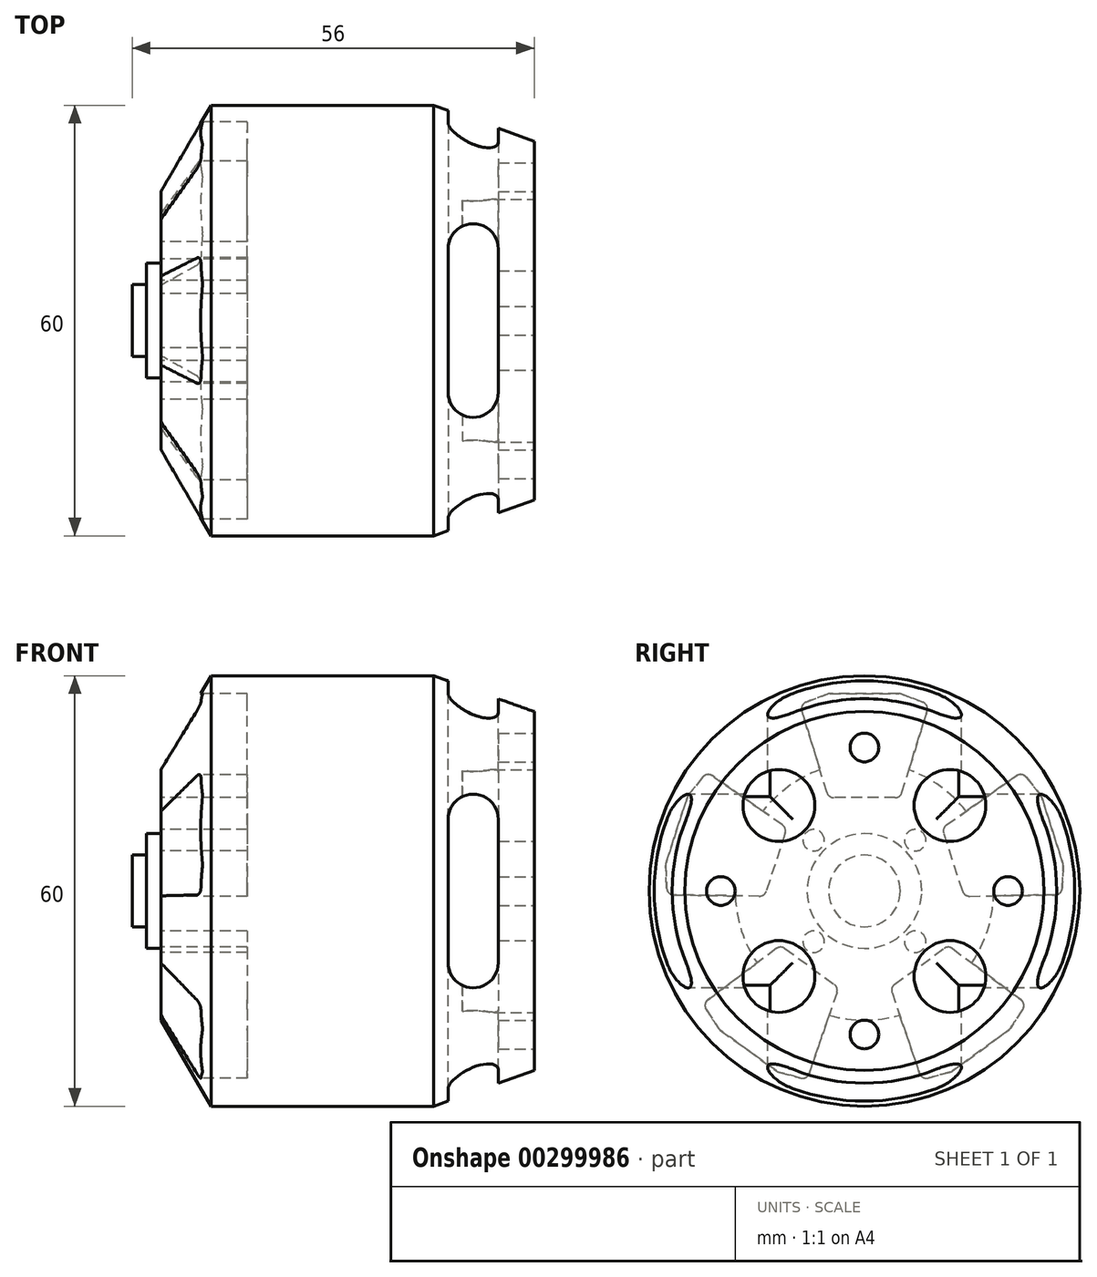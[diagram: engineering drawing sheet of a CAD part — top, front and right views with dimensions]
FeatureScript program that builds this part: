
annotation { "Feature Type Name" : "Feature", "Feature Type Description" : "" }
export const myFeature = defineFeature(function(context is Context, id is Id, definition is map)
    precondition{}
    {
        {
            var Q0;
            Q0=qCreatedBy(makeId("Right.planeOp"),FACE);
            var sketch = newSketch(context, id + "F0", { "sketchPlane" : qUnion([Q0])});
            skCircle(sketch, "E0", {"center": v(0, 0) * mm, "radius": 30 * mm});
            skSolve(sketch);
        }
        {
            var Q0;
            Q0 = qSketchRegion(id + "F0", true);
            extrude(context, id + "F1", {"entities" : qUnion([Q0]), "endBound" : BoundingType.SYMMETRIC, "depth" : 28 * mm, "offsetDistance" : 25 * mm});
        }
        {
            var Q0;
            Q0=qCreatedBy(makeId("Top.planeOp"),FACE);
            var sketch = newSketch(context, id + "F2", { "sketchPlane" : qUnion([Q0])});
            skLineSegment(sketch, "E1", {"start": v(14, 0) * mm, "end": v(28, 0) * mm});
            skLineSegment(sketch, "E2", {"start": v(14, 0) * mm, "end": v(14, 30) * mm});
            skLineSegment(sketch, "E3", {"start": v(14, 30) * mm, "end": v(28, 25) * mm});
            skLineSegment(sketch, "E4", {"start": v(28, 0) * mm, "end": v(28, 25) * mm});
            skLineSegment(sketch, "E5", {"start": v(-14, 0) * mm, "end": v(-24, 0) * mm});
            skLineSegment(sketch, "E6", {"start": v(-24, 0) * mm, "end": v(-24, 18) * mm});
            skLineSegment(sketch, "E7", {"start": v(-14, 0) * mm, "end": v(-14, 30) * mm});
            skLineSegment(sketch, "E8", {"start": v(-14, 30) * mm, "end": v(-17, 30) * mm});
            skLineSegment(sketch, "E9", {"start": v(-17, 30) * mm, "end": v(-24, 18) * mm});
            skLineSegment(sketch, "E10", {"start": v(-24, 0) * mm, "end": v(-26, 0) * mm});
            skLineSegment(sketch, "E11", {"start": v(-26, 0) * mm, "end": v(-26, 8) * mm});
            skLineSegment(sketch, "E12", {"start": v(-26, 8) * mm, "end": v(-24, 8) * mm});
            skLineSegment(sketch, "E13", {"start": v(-26, 0) * mm, "end": v(-28, 0) * mm});
            skLineSegment(sketch, "E14", {"start": v(-28, 0) * mm, "end": v(-28, 5) * mm});
            skLineSegment(sketch, "E15", {"start": v(-28, 5) * mm, "end": v(-26, 5) * mm});
            skSolve(sketch);
        }
        {
            var Q0;
            Q0 = qSketchRegion(id + "F2", true);
            var Q1;
            Q1=sQuery(id+"F2.wireOp",EDGE,"E1");
            revolve(context, id + "F3", {"operationType" : NewBodyOperationType.ADD, "entities" : qUnion([Q0]), "axis" : qUnion([Q1]), "revolveType" : RevolveType.FULL});
        }
        {
            var Q0;
            Q0=makeQuery(id+"F3.opRevolve","SWEPT_FACE",FACE,{"disambiguationData":[OSD([sQuery(id+"F2.wireOp",EDGE,"E4")])]});
            var sketch = newSketch(context, id + "F4", { "sketchPlane" : qUnion([Q0])});
            skCircle(sketch, "E16", {"center": v(0, 20) * mm, "radius": 2 * mm});
            skCircle(sketch, "E17", {"center": v(20, 0) * mm, "radius": 2 * mm});
            skCircle(sketch, "E18", {"center": v(0, -20) * mm, "radius": 2 * mm});
            skCircle(sketch, "E19", {"center": v(-20, 0) * mm, "radius": 2 * mm});
            skLineSegment(sketch, "E20", {"start": v(0, 0) * mm, "end": v(-11.92, 11.92) * mm});
            skCircle(sketch, "E21", {"center": v(-11.92, 11.92) * mm, "radius": 5 * mm});
            skCircle(sketch, "E22.1.0", {"center": v(-11.92, -11.92) * mm, "radius": 5 * mm});
            skCircle(sketch, "E22.2.0", {"center": v(11.92, -11.92) * mm, "radius": 5 * mm});
            skCircle(sketch, "E22.3.0", {"center": v(11.92, 11.92) * mm, "radius": 5 * mm});
            skPoint(sketch, "E22.center", {"position": v(0, 0) * mm});
            skSolve(sketch);
        }
        {
            var Q0;
            Q0 = qSketchRegion(id + "F4", true);
            extrude(context, id + "F5", {"entities" : qUnion([Q0]), "operationType" : NewBodyOperationType.REMOVE, "oppositeDirection" : true, "depth" : 10 * mm, "offsetDistance" : 25 * mm});
        }
        {
            var Q0;
            Q0=makeQuery(id+"F3.opRevolve","SWEPT_FACE",FACE,{"disambiguationData":[OSD([sQuery(id+"F2.wireOp",EDGE,"E6")])]});
            var sketch = newSketch(context, id + "F6", { "sketchPlane" : qUnion([Q0])});
            skLineSegment(sketch, "E23", {"start": v(0, 0) * mm, "end": v(7.07, 7.07) * mm});
            skCircle(sketch, "E24", {"center": v(7.07, 7.07) * mm, "radius": 1.5 * mm});
            skCircle(sketch, "E25.1.0", {"center": v(-7.07, 7.07) * mm, "radius": 1.5 * mm});
            skCircle(sketch, "E25.2.0", {"center": v(-7.07, -7.07) * mm, "radius": 1.5 * mm});
            skCircle(sketch, "E25.3.0", {"center": v(7.07, -7.07) * mm, "radius": 1.5 * mm});
            skPoint(sketch, "E25.center", {"position": v(0, 0) * mm});
            skLineSegment(sketch, "E26.bottom", {"start": v(-4.26, 13) * mm, "end": v(4.26, 13) * mm});
            skLineSegment(sketch, "E26.top", {"start": v(-4.82, 27.5) * mm, "end": v(4.82, 27.5) * mm});
            skLineSegment(sketch, "E26.left", {"start": v(-5, 13) * mm, "end": v(-5, 27.5) * mm});
            skLineSegment(sketch, "E26.right", {"start": v(5, 13) * mm, "end": v(5, 27.5) * mm});
            skLineSegment(sketch, "E27", {"start": v(5.22, 13.7) * mm, "end": v(8.72, 25.1) * mm});
            skLineSegment(sketch, "E28", {"start": v(8.12, 26.33) * mm, "end": v(5.17, 27.44) * mm});
            skLineSegment(sketch, "E29", {"start": v(-5.22, 13.7) * mm, "end": v(-8.72, 25.1) * mm});
            skLineSegment(sketch, "E30", {"start": v(-8.12, 26.33) * mm, "end": v(-5.17, 27.44) * mm});
            skPoint(sketch, "E31.visualSharp", {"position": v(9, 26) * mm});
            skArc(sketch, "E31.filletArc", {"start": v(8.72, 25.1) * mm, "mid": v(8.66, 25.84) * mm, "end": v(8.12, 26.33) * mm});
            skPoint(sketch, "E32.visualSharp", {"position": v(-9, 26) * mm});
            skArc(sketch, "E32.filletArc", {"start": v(-8.12, 26.33) * mm, "mid": v(-8.66, 25.84) * mm, "end": v(-8.72, 25.1) * mm});
            skPoint(sketch, "E33.visualSharp", {"position": v(-5, 13) * mm});
            skArc(sketch, "E33.filletArc", {"start": v(-5.22, 13.7) * mm, "mid": v(-4.86, 13.2) * mm, "end": v(-4.26, 13) * mm});
            skPoint(sketch, "E34.visualSharp", {"position": v(5, 13) * mm});
            skArc(sketch, "E34.filletArc", {"start": v(4.26, 13) * mm, "mid": v(4.86, 13.2) * mm, "end": v(5.22, 13.7) * mm});
            skPoint(sketch, "E35.visualSharp", {"position": v(5, 27.5) * mm});
            skArc(sketch, "E35.filletArc", {"start": v(5.17, 27.44) * mm, "mid": v(5, 27.48) * mm, "end": v(4.82, 27.5) * mm});
            skPoint(sketch, "E36.visualSharp", {"position": v(-5, 27.5) * mm});
            skArc(sketch, "E36.filletArc", {"start": v(-4.82, 27.5) * mm, "mid": v(-5, 27.48) * mm, "end": v(-5.17, 27.44) * mm});
            skLineSegment(sketch, "E37.1.0", {"start": v(-27.64, 3.92) * mm, "end": v(-24.67, 13.08) * mm});
            skLineSegment(sketch, "E37.1.1", {"start": v(-27.55, 0.42) * mm, "end": v(-27.7, 3.56) * mm});
            skArc(sketch, "E37.1.2", {"start": v(-27.55, 0.42) * mm, "mid": v(-27.25, -0.26) * mm, "end": v(-26.57, -0.54) * mm});
            skLineSegment(sketch, "E37.1.3", {"start": v(-14.65, -0.73) * mm, "end": v(-26.57, -0.54) * mm});
            skArc(sketch, "E37.1.4", {"start": v(-14.65, -0.73) * mm, "mid": v(-14.05, -0.54) * mm, "end": v(-13.68, -0.04) * mm});
            skLineSegment(sketch, "E37.1.5", {"start": v(-13.68, -0.04) * mm, "end": v(-11.05, 8.07) * mm});
            skArc(sketch, "E37.1.6", {"start": v(-11.05, 8.07) * mm, "mid": v(-11.05, 8.7) * mm, "end": v(-11.42, 9.2) * mm});
            skLineSegment(sketch, "E37.1.7", {"start": v(-11.42, 9.2) * mm, "end": v(-21.18, 16.05) * mm});
            skLineSegment(sketch, "E37.1.8", {"start": v(-22.53, 15.86) * mm, "end": v(-24.5, 13.4) * mm});
            skArc(sketch, "E37.1.9", {"start": v(-21.18, 16.05) * mm, "mid": v(-21.9, 16.22) * mm, "end": v(-22.53, 15.86) * mm});
            skArc(sketch, "E37.1.10", {"start": v(-24.5, 13.4) * mm, "mid": v(-24.6, 13.25) * mm, "end": v(-24.67, 13.08) * mm});
            skArc(sketch, "E37.1.11", {"start": v(-27.64, 3.92) * mm, "mid": v(-27.68, 3.74) * mm, "end": v(-27.7, 3.56) * mm});
            skLineSegment(sketch, "E37.2.0", {"start": v(-12.27, -25.08) * mm, "end": v(-20.06, -19.42) * mm});
            skLineSegment(sketch, "E37.2.1", {"start": v(-8.9, -26.07) * mm, "end": v(-11.94, -25.24) * mm});
            skArc(sketch, "E37.2.2", {"start": v(-8.9, -26.07) * mm, "mid": v(-8.18, -26) * mm, "end": v(-7.7, -25.43) * mm});
            skLineSegment(sketch, "E37.2.3", {"start": v(-3.84, -14.15) * mm, "end": v(-7.7, -25.43) * mm});
            skArc(sketch, "E37.2.4", {"start": v(-3.84, -14.15) * mm, "mid": v(-3.83, -13.53) * mm, "end": v(-4.2, -13.02) * mm});
            skLineSegment(sketch, "E37.2.5", {"start": v(-4.2, -13.02) * mm, "end": v(-11.09, -8.01) * mm});
            skArc(sketch, "E37.2.6", {"start": v(-11.09, -8.01) * mm, "mid": v(-11.68, -7.82) * mm, "end": v(-12.28, -8.02) * mm});
            skLineSegment(sketch, "E37.2.7", {"start": v(-12.28, -8.02) * mm, "end": v(-21.81, -15.18) * mm});
            skLineSegment(sketch, "E37.2.8", {"start": v(-22.04, -16.53) * mm, "end": v(-20.3, -19.16) * mm});
            skArc(sketch, "E37.2.9", {"start": v(-21.81, -15.18) * mm, "mid": v(-22.2, -15.8) * mm, "end": v(-22.04, -16.53) * mm});
            skArc(sketch, "E37.2.10", {"start": v(-20.3, -19.16) * mm, "mid": v(-20.2, -19.3) * mm, "end": v(-20.06, -19.42) * mm});
            skArc(sketch, "E37.2.11", {"start": v(-12.27, -25.08) * mm, "mid": v(-12.11, -25.17) * mm, "end": v(-11.94, -25.24) * mm});
            skLineSegment(sketch, "E37.3.0", {"start": v(20.06, -19.42) * mm, "end": v(12.27, -25.08) * mm});
            skLineSegment(sketch, "E37.3.1", {"start": v(22.04, -16.53) * mm, "end": v(20.3, -19.16) * mm});
            skArc(sketch, "E37.3.2", {"start": v(22.04, -16.53) * mm, "mid": v(22.2, -15.8) * mm, "end": v(21.81, -15.18) * mm});
            skLineSegment(sketch, "E37.3.3", {"start": v(12.28, -8.02) * mm, "end": v(21.81, -15.18) * mm});
            skArc(sketch, "E37.3.4", {"start": v(12.28, -8.02) * mm, "mid": v(11.68, -7.82) * mm, "end": v(11.09, -8.01) * mm});
            skLineSegment(sketch, "E37.3.5", {"start": v(11.09, -8.01) * mm, "end": v(4.2, -13.02) * mm});
            skArc(sketch, "E37.3.6", {"start": v(4.2, -13.02) * mm, "mid": v(3.83, -13.53) * mm, "end": v(3.84, -14.15) * mm});
            skLineSegment(sketch, "E37.3.7", {"start": v(3.84, -14.15) * mm, "end": v(7.7, -25.43) * mm});
            skLineSegment(sketch, "E37.3.8", {"start": v(8.9, -26.07) * mm, "end": v(11.94, -25.24) * mm});
            skArc(sketch, "E37.3.9", {"start": v(7.7, -25.43) * mm, "mid": v(8.18, -26) * mm, "end": v(8.9, -26.07) * mm});
            skArc(sketch, "E37.3.10", {"start": v(11.94, -25.24) * mm, "mid": v(12.11, -25.17) * mm, "end": v(12.27, -25.08) * mm});
            skArc(sketch, "E37.3.11", {"start": v(20.06, -19.42) * mm, "mid": v(20.2, -19.3) * mm, "end": v(20.3, -19.16) * mm});
            skLineSegment(sketch, "E37.4.0", {"start": v(24.67, 13.08) * mm, "end": v(27.64, 3.92) * mm});
            skLineSegment(sketch, "E37.4.1", {"start": v(22.53, 15.86) * mm, "end": v(24.5, 13.4) * mm});
            skArc(sketch, "E37.4.2", {"start": v(22.53, 15.86) * mm, "mid": v(21.9, 16.22) * mm, "end": v(21.18, 16.05) * mm});
            skLineSegment(sketch, "E37.4.3", {"start": v(11.42, 9.2) * mm, "end": v(21.18, 16.05) * mm});
            skArc(sketch, "E37.4.4", {"start": v(11.42, 9.2) * mm, "mid": v(11.05, 8.7) * mm, "end": v(11.05, 8.07) * mm});
            skLineSegment(sketch, "E37.4.5", {"start": v(11.05, 8.07) * mm, "end": v(13.68, -0.04) * mm});
            skArc(sketch, "E37.4.6", {"start": v(13.68, -0.04) * mm, "mid": v(14.05, -0.54) * mm, "end": v(14.65, -0.73) * mm});
            skLineSegment(sketch, "E37.4.7", {"start": v(14.65, -0.73) * mm, "end": v(26.57, -0.54) * mm});
            skLineSegment(sketch, "E37.4.8", {"start": v(27.55, 0.42) * mm, "end": v(27.7, 3.56) * mm});
            skArc(sketch, "E37.4.9", {"start": v(26.57, -0.54) * mm, "mid": v(27.25, -0.26) * mm, "end": v(27.55, 0.42) * mm});
            skArc(sketch, "E37.4.10", {"start": v(27.7, 3.56) * mm, "mid": v(27.68, 3.74) * mm, "end": v(27.64, 3.92) * mm});
            skArc(sketch, "E37.4.11", {"start": v(24.67, 13.08) * mm, "mid": v(24.6, 13.25) * mm, "end": v(24.5, 13.4) * mm});
            skSolve(sketch);
        }
        {
            var Q0;
            Q0 = qSketchRegion(id + "F6", true);
            extrude(context, id + "F7", {"entities" : qUnion([Q0]), "operationType" : NewBodyOperationType.REMOVE, "oppositeDirection" : true, "depth" : 12 * mm, "offsetDistance" : 25 * mm});
        }
        {
            var Q0;
            Q0=qCreatedBy(makeId("Front.planeOp"),FACE);
            var sketch = newSketch(context, id + "F8", { "sketchPlane" : qUnion([Q0])});
            skLineSegment(sketch, "E38.bottom", {"start": v(16, 10) * mm, "end": v(23, 10) * mm});
            skLineSegment(sketch, "E38.top", {"start": v(16, -10) * mm, "end": v(23, -10) * mm});
            skLineSegment(sketch, "E38.left", {"start": v(16, 10) * mm, "end": v(16, -10) * mm});
            skLineSegment(sketch, "E38.right", {"start": v(23, 10) * mm, "end": v(23, -10) * mm});
            skCircle(sketch, "E39", {"center": v(19.5, 10) * mm, "radius": 3.5 * mm});
            skCircle(sketch, "E40", {"center": v(19.5, -10) * mm, "radius": 3.5 * mm});
            skSolve(sketch);
        }
        {
            var Q0;
            Q0 = qSketchRegion(id + "F8", true);
            extrude(context, id + "F9", {"entities" : qUnion([Q0]), "operationType" : NewBodyOperationType.REMOVE, "endBound" : BoundingType.SYMMETRIC, "oppositeDirection" : true, "depth" : 65 * mm, "offsetDistance" : 25 * mm});
        }
        {
            var Q0;
            Q0=qCreatedBy(makeId("Top.planeOp"),FACE);
            var sketch = newSketch(context, id + "F10", { "sketchPlane" : qUnion([Q0])});
            skLineSegment(sketch, "E41.bottom", {"start": v(16, 10) * mm, "end": v(23, 10) * mm});
            skLineSegment(sketch, "E41.top", {"start": v(16, -10) * mm, "end": v(23, -10) * mm});
            skLineSegment(sketch, "E41.left", {"start": v(16, 10) * mm, "end": v(16, -10) * mm});
            skLineSegment(sketch, "E41.right", {"start": v(23, 10) * mm, "end": v(23, -10) * mm});
            skCircle(sketch, "E42", {"center": v(19.5, 10) * mm, "radius": 3.5 * mm});
            skCircle(sketch, "E43", {"center": v(19.5, -10) * mm, "radius": 3.5 * mm});
            skSolve(sketch);
        }
        {
            var Q0;
            Q0 = qSketchRegion(id + "F10", true);
            extrude(context, id + "F11", {"entities" : qUnion([Q0]), "operationType" : NewBodyOperationType.REMOVE, "endBound" : BoundingType.SYMMETRIC, "oppositeDirection" : true, "depth" : 65 * mm, "offsetDistance" : 25 * mm});
        }
    });
